# Revit family: Heve skyvedør Alu
name_source: partatom
category: Doors
revit_build: Autodesk Revit 2017 (Build: 20160225_1515(x64)
units: mm (PartAtom-declared; Revit-internal decimal feet)

## family parameters
Always vertical = Yes
Cut with Voids When Loaded = No
Host = Wall
OmniClass Number = 23.30.10.00
OmniClass Title = Doors
Room Calculation Point = Yes
Shared = No

## types (1)
- Heve skyvedør Alu
    Center = 906 mm
    Desire Height = 2118 mm
    Desire Width = 1788 mm
    Frame Material = <By Category>
    Function = Interior
    Glass = Glass
    Height = 2118 mm
    Joint = 12 mm  [stored 0.0393701 ft]
    Manufacturer = Dovista
    Model = GSD 1 leaf Alu 54 mm Pane
    Placement in wall = 50 mm  [stored 0.164042 ft]
    Rail = No
    Rough Height = 2142 mm  [stored 7.02756 ft]
    Rough Width = 1812 mm
    Wall Closure = By host
    Wall closure = 150 mm
    Width = 1788 mm

note: [stored X ft] marks values corroborated as IEEE doubles in the binary element streams (Revit-internal decimal feet)

## geometry (parser evidence)
native form markers: Sweep x3
no freeform markers — native parametric forms only
